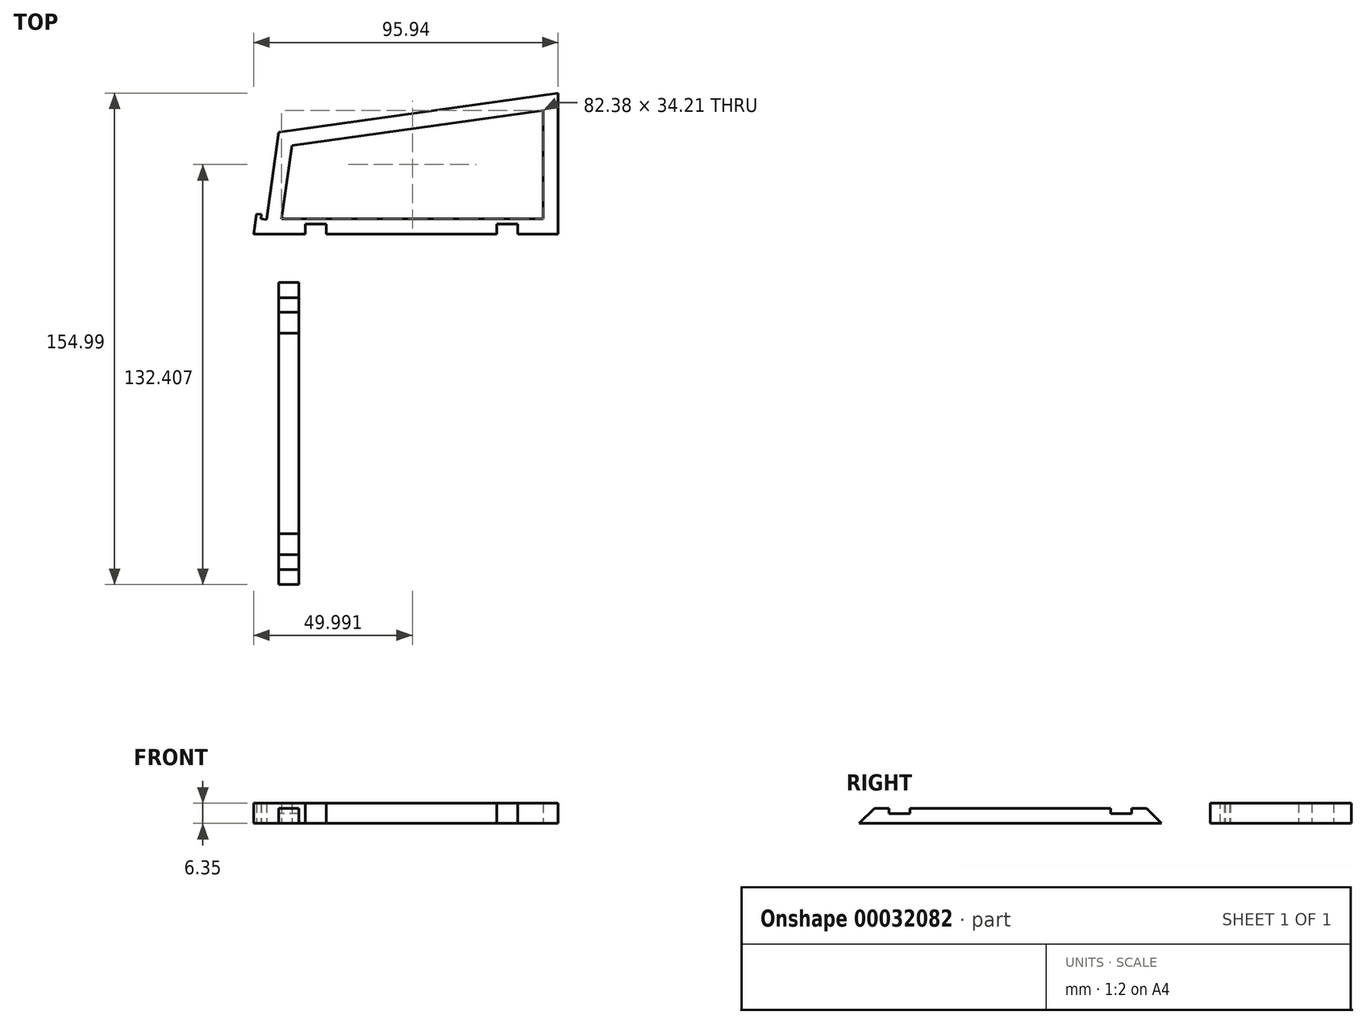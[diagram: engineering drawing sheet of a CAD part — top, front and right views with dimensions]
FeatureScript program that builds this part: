
annotation { "Feature Type Name" : "Feature", "Feature Type Description" : "" }
export const myFeature = defineFeature(function(context is Context, id is Id, definition is map)
    precondition{}
    {
        {
            var Q0;
            Q0=qCreatedBy(makeId("Front.planeOp"),FACE);
            var sketch = newSketch(context, id + "F0", { "sketchPlane" : qUnion([Q0])});
            skLineSegment(sketch, "E0", {"start": v(0, 0) * mm, "end": v(88.03, 12.37) * mm});
            skLineSegment(sketch, "E1", {"start": v(88.03, 12.37) * mm, "end": v(88.03, -32.08) * mm});
            skLineSegment(sketch, "E2", {"start": v(88.03, -32.08) * mm, "end": v(-7.9, -32.08) * mm});
            skLineSegment(sketch, "E3", {"start": v(-7.9, -32.08) * mm, "end": v(-7.01, -25.73) * mm});
            skLineSegment(sketch, "E4", {"start": v(-7.01, -25.73) * mm, "end": v(-5.44, -25.95) * mm});
            skLineSegment(sketch, "E5", {"start": v(-5.44, -25.95) * mm, "end": v(-5.63, -27.32) * mm});
            skLineSegment(sketch, "E6", {"start": v(-5.63, -27.32) * mm, "end": v(-3.87, -27.56) * mm});
            skLineSegment(sketch, "E7", {"start": v(-3.87, -27.56) * mm, "end": v(0, 0) * mm});
            skLineSegment(sketch, "E8.0", {"start": v(83.27, -27.32) * mm, "end": v(0.89, -27.32) * mm});
            skLineSegment(sketch, "E8.1", {"start": v(83.27, 6.9) * mm, "end": v(83.27, -27.32) * mm});
            skLineSegment(sketch, "E8.2", {"start": v(4.13, -4.23) * mm, "end": v(83.27, 6.9) * mm});
            skLineSegment(sketch, "E9", {"start": v(4.13, -4.23) * mm, "end": v(0.89, -27.32) * mm});
            skSolve(sketch);
        }
        {
            var Q0;
            Q0 = qSketchRegion(id + "F0", true);
            extrude(context, id + "F1", {"entities" : qUnion([Q0]), "depth" : 6.35 * mm});
        }
        {
            var Q0;
            Q0=makeQuery(id+"F1.opExtrude","CAP_FACE",FACE,{"disambiguationData":[OSD([sQuery(id+"F0.wireOp",EDGE,"E0"),sQuery(id+"F0.wireOp",EDGE,"E1"),sQuery(id+"F0.wireOp",EDGE,"E2"),sQuery(id+"F0.wireOp",EDGE,"E3"),sQuery(id+"F0.wireOp",EDGE,"E4"),sQuery(id+"F0.wireOp",EDGE,"E5"),sQuery(id+"F0.wireOp",EDGE,"E6"),sQuery(id+"F0.wireOp",EDGE,"E7"),sQuery(id+"F0.wireOp",EDGE,"E8.0"),sQuery(id+"F0.wireOp",EDGE,"E8.1"),sQuery(id+"F0.wireOp",EDGE,"E8.2"),sQuery(id+"F0.wireOp",EDGE,"E9")])],"isStart":false});
            var sketch = newSketch(context, id + "F2", { "sketchPlane" : qUnion([Q0])});
            skLineSegment(sketch, "E10.bottom", {"start": v(8.4, -32.08) * mm, "end": v(15, -32.08) * mm});
            skLineSegment(sketch, "E10.top", {"start": v(8.4, -28.9) * mm, "end": v(15, -28.9) * mm});
            skLineSegment(sketch, "E10.left", {"start": v(8.4, -32.08) * mm, "end": v(8.4, -28.9) * mm});
            skLineSegment(sketch, "E10.right", {"start": v(15, -32.08) * mm, "end": v(15, -28.9) * mm});
            skLineSegment(sketch, "E11.bottom", {"start": v(68.73, -32.08) * mm, "end": v(75.33, -32.08) * mm});
            skLineSegment(sketch, "E11.top", {"start": v(68.73, -28.9) * mm, "end": v(75.33, -28.9) * mm});
            skLineSegment(sketch, "E11.left", {"start": v(68.73, -32.08) * mm, "end": v(68.73, -28.9) * mm});
            skLineSegment(sketch, "E11.right", {"start": v(75.33, -32.08) * mm, "end": v(75.33, -28.9) * mm});
            skSolve(sketch);
        }
        {
            var Q0;
            Q0 = qSketchRegion(id + "F2", true);
            extrude(context, id + "F3", {"entities" : qUnion([Q0]), "operationType" : NewBodyOperationType.REMOVE, "oppositeDirection" : true, "depth" : 25.4 * mm});
        }
        {
            var Q0;
            Q0=qCreatedBy(makeId("Right.planeOp"),FACE);
            var sketch = newSketch(context, id + "F4", { "sketchPlane" : qUnion([Q0])});
            skLineSegment(sketch, "E12.bottom", {"start": v(-15.29, -32.08) * mm, "end": v(-110.54, -32.08) * mm});
            skLineSegment(sketch, "E12.top", {"start": v(-20.05, -27.32) * mm, "end": v(-24.68, -27.32) * mm});
            skLineSegment(sketch, "E13", {"start": v(-15.29, -32.08) * mm, "end": v(-20.05, -27.32) * mm});
            skLineSegment(sketch, "E14", {"start": v(-110.54, -32.08) * mm, "end": v(-105.77, -27.32) * mm});
            skLineSegment(sketch, "E15", {"start": v(-24.68, -27.32) * mm, "end": v(-24.68, -29.03) * mm});
            skLineSegment(sketch, "E16", {"start": v(-24.68, -29.03) * mm, "end": v(-31.29, -29.03) * mm});
            skLineSegment(sketch, "E17", {"start": v(-31.29, -29.03) * mm, "end": v(-31.29, -27.32) * mm});
            skLineSegment(sketch, "E18.trimOffspring", {"start": v(-31.29, -27.32) * mm, "end": v(-94.53, -27.32) * mm});
            skLineSegment(sketch, "E19", {"start": v(-62.91, -32.08) * mm, "end": v(-62.91, -27.32) * mm, "construction": true});
            skLineSegment(sketch, "E20.top", {"start": v(-94.53, -29.03) * mm, "end": v(-101.14, -29.03) * mm});
            skLineSegment(sketch, "E20.left", {"start": v(-94.53, -27.32) * mm, "end": v(-94.53, -29.03) * mm});
            skLineSegment(sketch, "E20.right", {"start": v(-101.14, -27.32) * mm, "end": v(-101.14, -29.03) * mm});
            skLineSegment(sketch, "E21.trimOffspring", {"start": v(-101.14, -27.32) * mm, "end": v(-105.77, -27.32) * mm});
            skSolve(sketch);
        }
        {
            var Q0;
            Q0 = qSketchRegion(id + "F4", true);
            extrude(context, id + "F5", {"entities" : qUnion([Q0]), "depth" : 6.35 * mm});
        }
        {
            var Q0;
            Q0=makeQuery(id+"F1.opExtrude","SWEPT_BODY",BODY,{"disambiguationData":[OSD([sQuery(id+"F0.wireOp",EDGE,"E0"),sQuery(id+"F0.wireOp",EDGE,"E1"),sQuery(id+"F0.wireOp",EDGE,"E2"),sQuery(id+"F0.wireOp",EDGE,"E3"),sQuery(id+"F0.wireOp",EDGE,"E4"),sQuery(id+"F0.wireOp",EDGE,"E5"),sQuery(id+"F0.wireOp",EDGE,"E6"),sQuery(id+"F0.wireOp",EDGE,"E7"),sQuery(id+"F0.wireOp",EDGE,"E8.0"),sQuery(id+"F0.wireOp",EDGE,"E8.1"),sQuery(id+"F0.wireOp",EDGE,"E8.2"),sQuery(id+"F0.wireOp",EDGE,"E9")])]});
            var Q1;
            {var subQ0=sQuery(id+"F0.wireOp",EDGE,"E2");Q1=makeQuery(id+"F3.boolean.opBoolean","SPLIT",EDGE,{"disambiguationData":[TD([makeQuery(id+"F3.opExtrude","SWEPT_FACE",FACE,{"disambiguationData":[OSD([sQuery(id+"F2.wireOp",EDGE,"E10.right")])]})])],"derivedFrom":makeQuery(id+"F1.opExtrude","CAP_EDGE",EDGE,{"disambiguationData":[OSD([subQ0])],"isStart":true})});}
            transform(context, id + "F6", {"entities" : qUnion([Q0]), "transformType" : TransformType.ROTATION, "transformAxis" : qUnion([Q1]), "angle" : 90 * degree, "makeCopy" : false});
        }
    });
